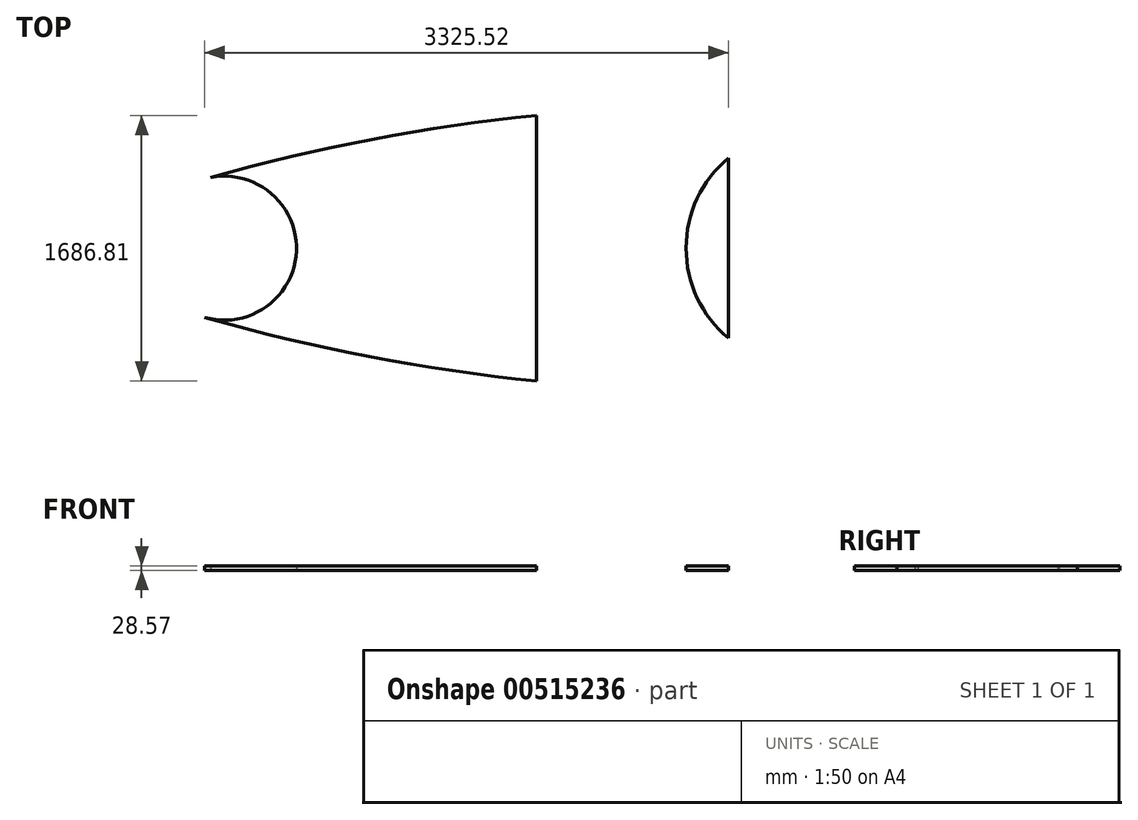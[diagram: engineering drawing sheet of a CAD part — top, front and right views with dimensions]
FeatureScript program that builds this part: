
annotation { "Feature Type Name" : "Feature", "Feature Type Description" : "" }
export const myFeature = defineFeature(function(context is Context, id is Id, definition is map)
    precondition{}
    {
        {
            var Q0;
            Q0=qCreatedBy(makeId("Top.planeOp"),FACE);
            var sketch = newSketch(context, id + "F0", { "sketchPlane" : qUnion([Q0])});
            skLineSegment(sketch, "E0.bottom", {"start": v(2438.4, 904.88) * mm, "end": v(-2438.4, 904.87) * mm});
            skLineSegment(sketch, "E0.top", {"start": v(2438.4, -904.87) * mm, "end": v(-2438.4, -904.88) * mm});
            skLineSegment(sketch, "E0.left", {"start": v(2438.4, 904.88) * mm, "end": v(2438.4, -904.87) * mm});
            skLineSegment(sketch, "E0.right", {"start": v(-2438.4, 904.87) * mm, "end": v(-2438.4, -904.88) * mm});
            skPoint(sketch, "E0.middle", {"position": v(0, 0) * mm});
            skLineSegment(sketch, "E1", {"start": v(-2438.4, 0) * mm, "end": v(2438.4, 0) * mm});
            skLineSegment(sketch, "E2", {"start": v(2438.4, -904.87) * mm, "end": v(1219.2, -904.88) * mm});
            skLineSegment(sketch, "E3", {"start": v(1219.2, -904.88) * mm, "end": v(0, -904.88) * mm});
            skLineSegment(sketch, "E4", {"start": v(0, -904.88) * mm, "end": v(-1219.2, -904.88) * mm});
            skLineSegment(sketch, "E5", {"start": v(-1219.2, -904.88) * mm, "end": v(-2438.4, -904.88) * mm});
            skLineSegment(sketch, "E6", {"start": v(-1219.2, -904.88) * mm, "end": v(-1219.2, 904.87) * mm});
            skLineSegment(sketch, "E7", {"start": v(0, -904.88) * mm, "end": v(0, 904.87) * mm});
            skLineSegment(sketch, "E8", {"start": v(1219.2, -904.88) * mm, "end": v(1219.2, 904.88) * mm});
            skLineSegment(sketch, "E9", {"start": v(-2438.4, 0) * mm, "end": v(-1981.2, 0) * mm});
            skCircle(sketch, "E10", {"center": v(-1981.2, 0) * mm, "radius": 457.2 * mm});
            skLineSegment(sketch, "E11", {"start": v(1219.2, 0) * mm, "end": v(1694.69, 0) * mm});
            skCircle(sketch, "E12", {"center": v(1694.69, 0) * mm, "radius": 743.71 * mm});
            skLineSegment(sketch, "E13", {"start": v(1219.2, 904.88) * mm, "end": v(1219.2, 619.13) * mm});
            skLineSegment(sketch, "E14", {"start": v(1219.2, -904.88) * mm, "end": v(1219.2, -619.12) * mm});
            skArc(sketch, "E15", {"start": v(1219.2, 904.88) * mm, "mid": v(1694.14, 828.98) * mm, "end": v(2121.77, 608.86) * mm});
            skArc(sketch, "E16", {"start": v(1219.2, -904.88) * mm, "mid": v(1694.14, -828.98) * mm, "end": v(2121.77, -608.86) * mm});
            skLineSegment(sketch, "E17", {"start": v(-2438.4, 904.87) * mm, "end": v(-2106.83, 904.87) * mm});
            skLineSegment(sketch, "E18", {"start": v(-2106.83, 904.87) * mm, "end": v(-2106.83, 438.05) * mm});
            skLineSegment(sketch, "E19", {"start": v(-2438.4, -904.88) * mm, "end": v(-2106.83, -904.88) * mm});
            skLineSegment(sketch, "E20", {"start": v(-2106.83, -904.88) * mm, "end": v(-2106.83, -439.6) * mm});
            skArc(sketch, "E21", {"start": v(1219.2, 904.88) * mm, "mid": v(-460.1, 787.52) * mm, "end": v(-2106.83, 438.05) * mm});
            skArc(sketch, "E22", {"start": v(-2106.83, -439.6) * mm, "mid": v(-460.05, -788.29) * mm, "end": v(1219.2, -904.87) * mm});
            skSolve(sketch);
        }
        {
            var Q0;
            {var subQ1=sQuery(id+"F0.wireOp",EDGE,"E9");Q0=makeQuery(id+"F0.imprint","IMPRINT",FACE,{"disambiguationData":[TD([[makeQuery(id+"F0.imprint","IMPRINT",EDGE,{"derivedFrom":subQ1}),1.0]])]});}
            var Q1;
            {var subQ7=sQuery(id+"F0.wireOp",EDGE,"E9");Q1=makeQuery(id+"F0.imprint","IMPRINT",FACE,{"disambiguationData":[TD([[makeQuery(id+"F0.imprint","IMPRINT",EDGE,{"derivedFrom":subQ7}),-1.0]])]});}
            var Q2;
            {var subQ0=sQuery(id+"F0.wireOp",EDGE,"E10");var subQ1=sQuery(id+"F0.wireOp",EDGE,"E1");var subQ2=makeQuery(id+"F0.imprint","INTERSECT",VERTEX,{"derivedFrom":[subQ1,subQ0]});Q2=makeQuery(id+"F0.imprint","IMPRINT",FACE,{"disambiguationData":[TD([[makeQuery(id+"F0.imprint","IMPRINT",EDGE,{"disambiguationData":[TD([[subQ2,-1.0]])],"derivedFrom":subQ1}),1.0]])]});}
            var Q3;
            {var subQ0=sQuery(id+"F0.wireOp",EDGE,"E10");var subQ1=sQuery(id+"F0.wireOp",EDGE,"E1");var subQ2=makeQuery(id+"F0.imprint","INTERSECT",VERTEX,{"derivedFrom":[subQ1,subQ0]});Q3=makeQuery(id+"F0.imprint","IMPRINT",FACE,{"disambiguationData":[TD([[makeQuery(id+"F0.imprint","IMPRINT",EDGE,{"disambiguationData":[TD([[subQ2,-1.0]])],"derivedFrom":subQ1}),-1.0]])]});}
            var Q4;
            {var subQ0=sQuery(id+"F0.wireOp",EDGE,"E6");var subQ1=sQuery(id+"F0.wireOp",EDGE,"E1");var subQ2=makeQuery(id+"F0.imprint","INTERSECT",VERTEX,{"derivedFrom":[subQ1,subQ0]});Q4=makeQuery(id+"F0.imprint","IMPRINT",FACE,{"disambiguationData":[TD([[makeQuery(id+"F0.imprint","IMPRINT",EDGE,{"disambiguationData":[TD([[subQ2,-1.0]])],"derivedFrom":subQ1}),-1.0]])]});}
            var Q5;
            {var subQ0=sQuery(id+"F0.wireOp",EDGE,"E6");var subQ1=sQuery(id+"F0.wireOp",EDGE,"E1");var subQ2=makeQuery(id+"F0.imprint","INTERSECT",VERTEX,{"derivedFrom":[subQ1,subQ0]});Q5=makeQuery(id+"F0.imprint","IMPRINT",FACE,{"disambiguationData":[TD([[makeQuery(id+"F0.imprint","IMPRINT",EDGE,{"disambiguationData":[TD([[subQ2,-1.0]])],"derivedFrom":subQ1}),1.0]])]});}
            var Q6;
            {var subQ0=sQuery(id+"F0.wireOp",EDGE,"E13");Q6=makeQuery(id+"F0.imprint","IMPRINT",FACE,{"disambiguationData":[TD([[makeQuery(id+"F0.imprint","IMPRINT",EDGE,{"derivedFrom":subQ0}),-1.0]])]});}
            var Q7;
            {var subQ0=sQuery(id+"F0.wireOp",EDGE,"E14");Q7=makeQuery(id+"F0.imprint","IMPRINT",FACE,{"disambiguationData":[TD([[makeQuery(id+"F0.imprint","IMPRINT",EDGE,{"derivedFrom":subQ0}),1.0]])]});}
            var Q8;
            {var subQ1=sQuery(id+"F0.wireOp",EDGE,"E1");var subQ3=sQuery(id+"F0.wireOp",EDGE,"E12");var subQ4=makeQuery(id+"F0.imprint","INTERSECT",VERTEX,{"derivedFrom":[subQ1,subQ3]});Q8=makeQuery(id+"F0.imprint","IMPRINT",FACE,{"disambiguationData":[TD([[makeQuery(id+"F0.imprint","IMPRINT",EDGE,{"disambiguationData":[TD([[subQ4,-1.0]])],"derivedFrom":subQ3}),1.0]])]});}
            var Q9;
            {var subQ1=sQuery(id+"F0.wireOp",EDGE,"E1");var subQ3=sQuery(id+"F0.wireOp",EDGE,"E12");var subQ4=makeQuery(id+"F0.imprint","INTERSECT",VERTEX,{"derivedFrom":[subQ1,subQ3]});Q9=makeQuery(id+"F0.imprint","IMPRINT",FACE,{"disambiguationData":[TD([[makeQuery(id+"F0.imprint","IMPRINT",EDGE,{"disambiguationData":[TD([[subQ4,1.0]])],"derivedFrom":subQ3}),1.0]])]});}
            var Q10;
            {var subQ4=sQuery(id+"F0.wireOp",EDGE,"E11");Q10=makeQuery(id+"F0.imprint","IMPRINT",FACE,{"disambiguationData":[TD([[makeQuery(id+"F0.imprint","IMPRINT",EDGE,{"derivedFrom":subQ4}),1.0]])]});}
            var Q11;
            {var subQ0=sQuery(id+"F0.wireOp",EDGE,"E13");Q11=makeQuery(id+"F0.imprint","IMPRINT",FACE,{"disambiguationData":[TD([[makeQuery(id+"F0.imprint","IMPRINT",EDGE,{"derivedFrom":subQ0}),1.0]])]});}
            var Q12;
            {var subQ0=sQuery(id+"F0.wireOp",EDGE,"E14");Q12=makeQuery(id+"F0.imprint","IMPRINT",FACE,{"disambiguationData":[TD([[makeQuery(id+"F0.imprint","IMPRINT",EDGE,{"derivedFrom":subQ0}),-1.0]])]});}
            var Q13;
            {var subQ4=sQuery(id+"F0.wireOp",EDGE,"E11");Q13=makeQuery(id+"F0.imprint","IMPRINT",FACE,{"disambiguationData":[TD([[makeQuery(id+"F0.imprint","IMPRINT",EDGE,{"derivedFrom":subQ4}),-1.0]])]});}
            extrude(context, id + "F1", {"entities" : qUnion([Q0, Q1, Q2, Q3, Q4, Q5, Q6, Q7, Q8, Q9, Q10, Q11, Q12, Q13]), "depth" : 28.57 * mm});
        }
    });
